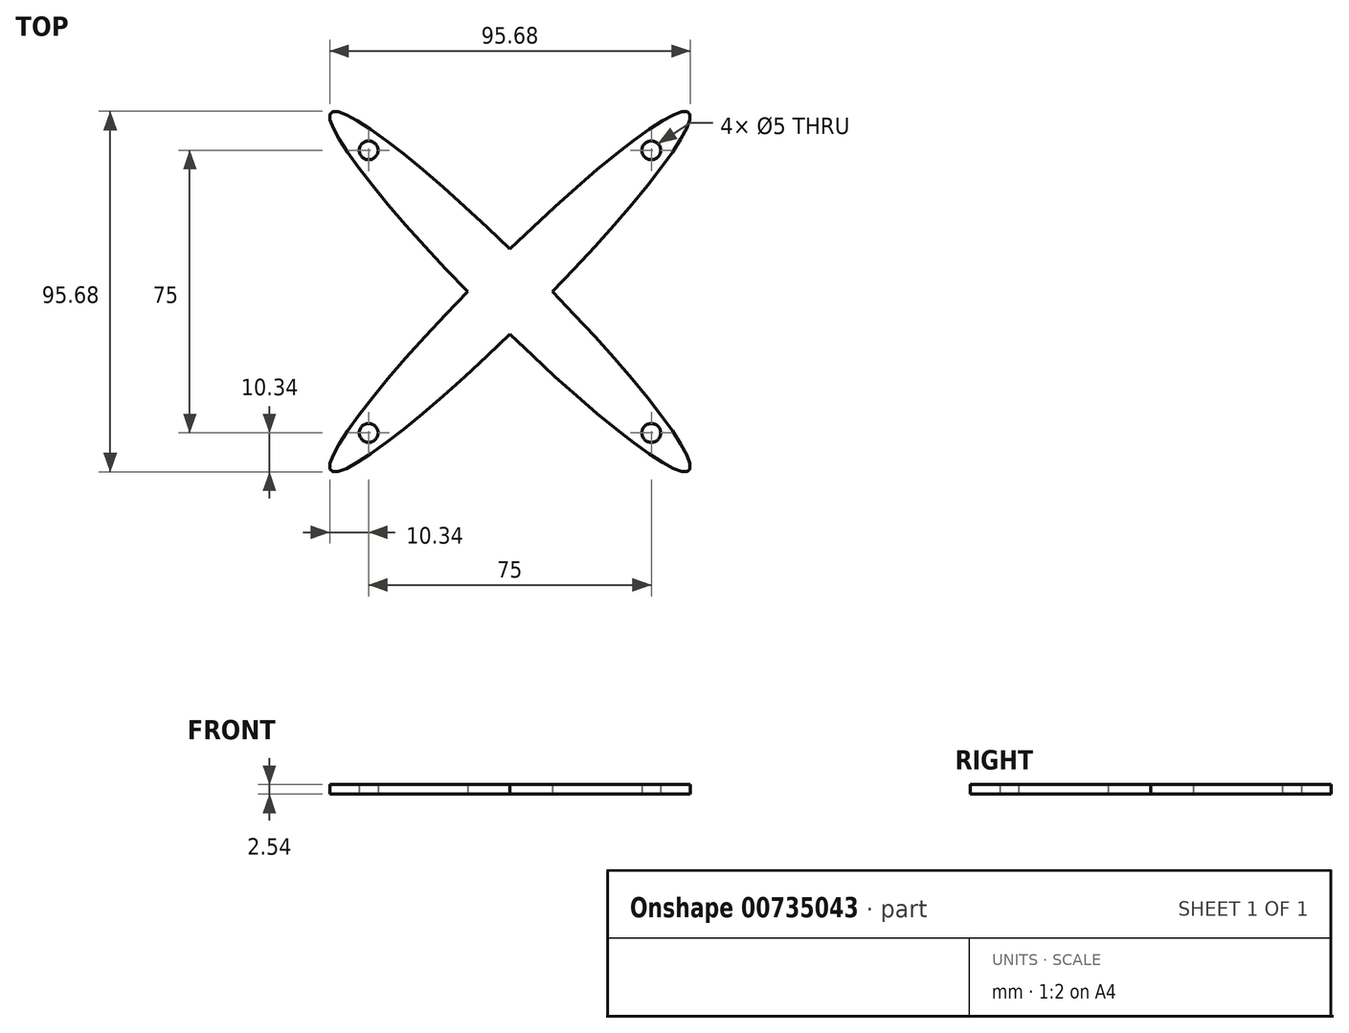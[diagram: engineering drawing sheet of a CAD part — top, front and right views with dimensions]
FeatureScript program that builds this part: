
annotation { "Feature Type Name" : "Feature", "Feature Type Description" : "" }
export const myFeature = defineFeature(function(context is Context, id is Id, definition is map)
    precondition{}
    {
        {
            var Q0;
            Q0=qCreatedBy(makeId("Top.planeOp"),FACE);
            var sketch = newSketch(context, id + "F0", { "sketchPlane" : qUnion([Q0])});
            skCircle(sketch, "E0", {"center": v(-37.5, -37.5) * mm, "radius": 2.5 * mm});
            skCircle(sketch, "E1", {"center": v(37.5, 37.5) * mm, "radius": 2.5 * mm});
            skEllipse(sketch, "E2", {"center": v(0, 0) * mm, "majorRadius": 67.18 * mm, "minorRadius": 8.03 * mm, "majorAxis": v(-0.7, -0.7)});
            skCircle(sketch, "E3", {"center": v(-37.5, 37.5) * mm, "radius": 2.5 * mm});
            skCircle(sketch, "E4", {"center": v(37.5, -37.5) * mm, "radius": 2.5 * mm});
            skEllipse(sketch, "E5", {"center": v(0, 0) * mm, "majorRadius": 67.18 * mm, "minorRadius": 8.03 * mm, "majorAxis": v(-0.7, 0.7)});
            skSolve(sketch);
        }
        {
            var Q0;
            Q0=makeQuery(id+"F0.imprint","IMPRINT",FACE,{"disambiguationData":[TD([[makeQuery(id+"F0.imprint","IMPRINT",EDGE,{"derivedFrom":sQuery(id+"F0.wireOp",EDGE,"E0")}),-1.0]])]});
            var Q1;
            Q1=makeQuery(id+"F0.imprint","IMPRINT",FACE,{"disambiguationData":[TD([[makeQuery(id+"F0.imprint","IMPRINT",EDGE,{"derivedFrom":sQuery(id+"F0.wireOp",EDGE,"E3")}),-1.0]])]});
            var Q2;
            Q2=makeQuery(id+"F0.imprint","IMPRINT",FACE,{"disambiguationData":[TD([[makeQuery(id+"F0.imprint","IMPRINT",EDGE,{"derivedFrom":sQuery(id+"F0.wireOp",EDGE,"E1")}),-1.0]])]});
            var Q3;
            Q3=makeQuery(id+"F0.imprint","IMPRINT",FACE,{"disambiguationData":[TD([[makeQuery(id+"F0.imprint","IMPRINT",EDGE,{"derivedFrom":sQuery(id+"F0.wireOp",EDGE,"E4")}),-1.0]])]});
            var Q4;
            {var subQ0=sQuery(id+"F0.wireOp",EDGE,"E5");var subQ1=sQuery(id+"F0.wireOp",EDGE,"E2");var subQ2=makeQuery(id+"F0.imprint","INTERSECT",VERTEX,{"disambiguationData":[OD(0.0)],"derivedFrom":[subQ1,subQ0]});Q4=makeQuery(id+"F0.imprint","IMPRINT",FACE,{"disambiguationData":[TD([[makeQuery(id+"F0.imprint","IMPRINT",EDGE,{"disambiguationData":[TD([[subQ2,1.0]])],"derivedFrom":subQ1}),1.0]])]});}
            extrude(context, id + "F1", {"entities" : qUnion([Q0, Q1, Q2, Q3, Q4]), "depth" : 2.54 * mm, "offsetDistance" : 25.4 * mm});
        }
    });
